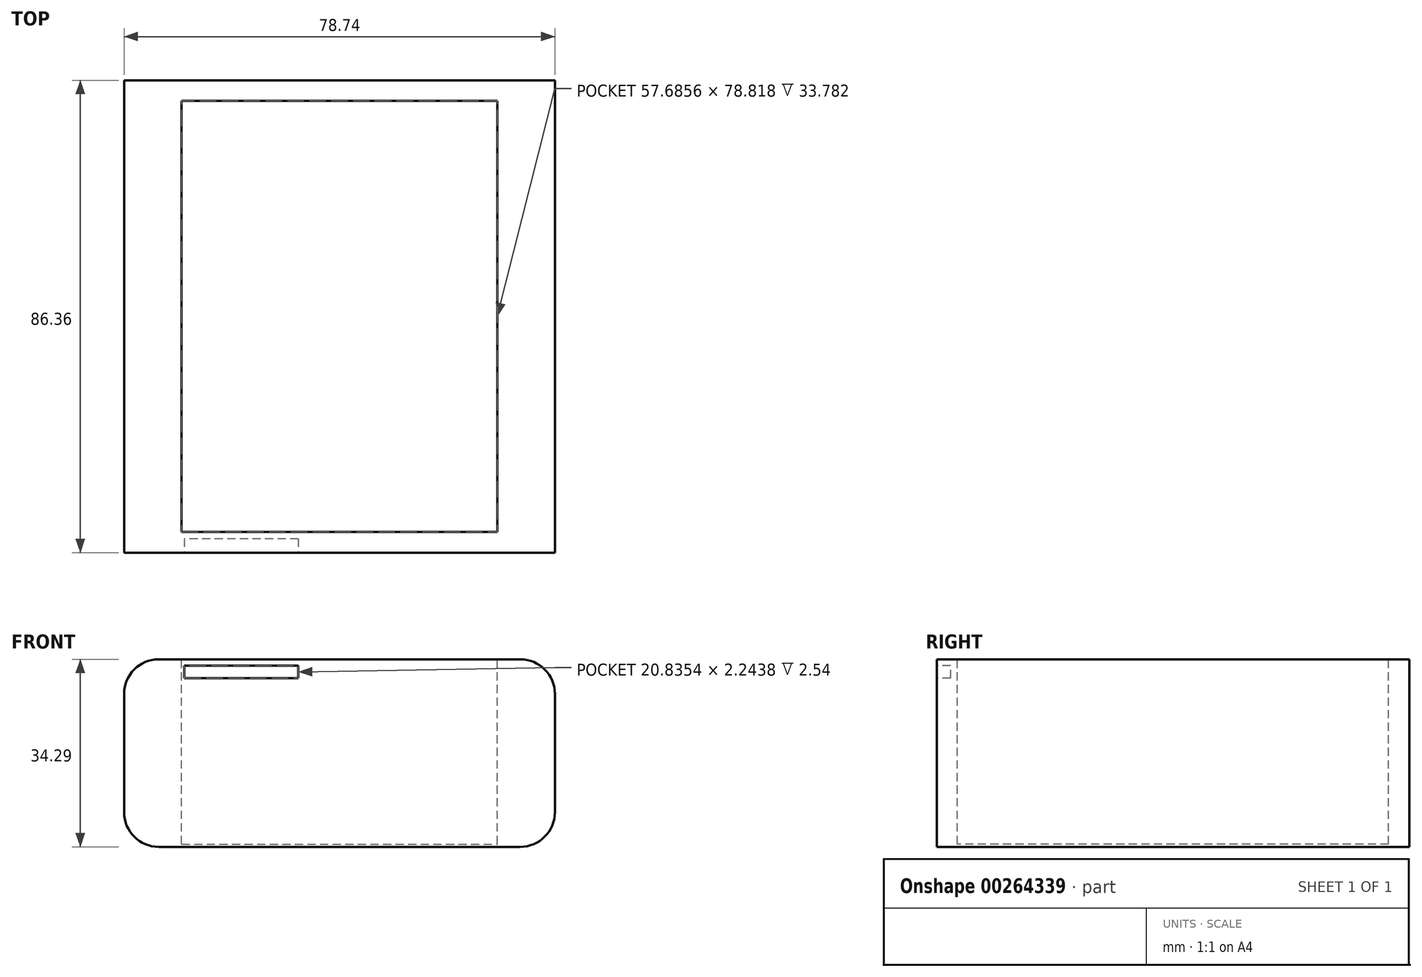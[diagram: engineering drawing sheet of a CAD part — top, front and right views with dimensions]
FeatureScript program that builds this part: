
annotation { "Feature Type Name" : "Feature", "Feature Type Description" : "" }
export const myFeature = defineFeature(function(context is Context, id is Id, definition is map)
    precondition{}
    {
        {
            var Q0;
            Q0=qCreatedBy(makeId("Front.planeOp"),FACE);
            var sketch = newSketch(context, id + "F0", { "sketchPlane" : qUnion([Q0])});
            skLineSegment(sketch, "E0.bottom", {"start": v(-33.02, -18.53) * mm, "end": v(33.02, -18.53) * mm});
            skLineSegment(sketch, "E0.top", {"start": v(-33.02, 15.76) * mm, "end": v(33.02, 15.76) * mm});
            skLineSegment(sketch, "E0.left", {"start": v(-39.37, -12.18) * mm, "end": v(-39.37, 9.4) * mm});
            skLineSegment(sketch, "E0.right", {"start": v(39.37, -12.18) * mm, "end": v(39.37, 9.4) * mm});
            skPoint(sketch, "E0.middle", {"position": v(0, -1.39) * mm});
            skPoint(sketch, "E1.visualSharp", {"position": v(-39.37, 15.76) * mm});
            skArc(sketch, "E1.filletArc", {"start": v(-33.02, 15.76) * mm, "mid": v(-37.51, 13.9) * mm, "end": v(-39.37, 9.4) * mm});
            skPoint(sketch, "E2.visualSharp", {"position": v(39.37, 15.76) * mm});
            skArc(sketch, "E2.filletArc", {"start": v(39.37, 9.4) * mm, "mid": v(37.51, 13.9) * mm, "end": v(33.02, 15.76) * mm});
            skPoint(sketch, "E3.visualSharp", {"position": v(39.37, -18.53) * mm});
            skArc(sketch, "E3.filletArc", {"start": v(33.02, -18.53) * mm, "mid": v(37.51, -16.67) * mm, "end": v(39.37, -12.18) * mm});
            skPoint(sketch, "E4.visualSharp", {"position": v(-39.37, -18.53) * mm});
            skArc(sketch, "E4.filletArc", {"start": v(-39.37, -12.18) * mm, "mid": v(-37.51, -16.67) * mm, "end": v(-33.02, -18.53) * mm});
            skSolve(sketch);
        }
        {
            var Q0;
            Q0=makeQuery(id+"F0.imprint","IMPRINT",FACE,{"disambiguationData":[TD([[makeQuery(id+"F0.imprint","IMPRINT",EDGE,{"derivedFrom":sQuery(id+"F0.wireOp",EDGE,"E0.bottom")}),1.0]])]});
            extrude(context, id + "F1", {"entities" : qUnion([Q0]), "endBound" : BoundingType.SYMMETRIC, "depth" : 86.36 * mm});
        }
        {
            var Q0;
            Q0=makeQuery(id+"F1.opExtrude","SWEPT_FACE",FACE,{"disambiguationData":[OSD([sQuery(id+"F0.wireOp",EDGE,"E0.top")])]});
            var sketch = newSketch(context, id + "F2", { "sketchPlane" : qUnion([Q0])});
            skLineSegment(sketch, "E5.bottom", {"start": v(-28.84, 39.4) * mm, "end": v(28.84, 39.4) * mm});
            skLineSegment(sketch, "E5.top", {"start": v(-28.84, -39.4) * mm, "end": v(28.84, -39.4) * mm});
            skLineSegment(sketch, "E5.left", {"start": v(-28.84, 39.4) * mm, "end": v(-28.84, -39.4) * mm});
            skLineSegment(sketch, "E5.right", {"start": v(28.84, 39.4) * mm, "end": v(28.84, -39.4) * mm});
            skPoint(sketch, "E5.middle", {"position": v(0, 0) * mm});
            skSolve(sketch);
        }
        {
            var Q0;
            Q0=makeQuery(id+"F2.imprint","IMPRINT",FACE,{"disambiguationData":[TD([[makeQuery(id+"F2.imprint","IMPRINT",EDGE,{"derivedFrom":sQuery(id+"F2.wireOp",EDGE,"E5.bottom")}),-1.0]])]});
            extrude(context, id + "F3", {"entities" : qUnion([Q0]), "operationType" : NewBodyOperationType.REMOVE, "oppositeDirection" : true, "depth" : 33.78 * mm});
        }
        {
            var Q0;
            Q0=makeQuery(id+"F1.opExtrude","CAP_FACE",FACE,{"disambiguationData":[OSD([sQuery(id+"F0.wireOp",EDGE,"E0.bottom"),sQuery(id+"F0.wireOp",EDGE,"E0.top"),sQuery(id+"F0.wireOp",EDGE,"E0.left"),sQuery(id+"F0.wireOp",EDGE,"E0.right"),sQuery(id+"F0.wireOp",EDGE,"E1.filletArc"),sQuery(id+"F0.wireOp",EDGE,"E2.filletArc"),sQuery(id+"F0.wireOp",EDGE,"E3.filletArc"),sQuery(id+"F0.wireOp",EDGE,"E4.filletArc")])],"isStart":false});
            var sketch = newSketch(context, id + "F4", { "sketchPlane" : qUnion([Q0])});
            skLineSegment(sketch, "E6.bottom", {"start": v(-7.5, 12.33) * mm, "end": v(-28.34, 12.33) * mm});
            skLineSegment(sketch, "E6.top", {"start": v(-7.5, 14.57) * mm, "end": v(-28.34, 14.57) * mm});
            skLineSegment(sketch, "E6.left", {"start": v(-7.5, 12.33) * mm, "end": v(-7.5, 14.57) * mm});
            skLineSegment(sketch, "E6.right", {"start": v(-28.34, 12.33) * mm, "end": v(-28.34, 14.57) * mm});
            skPoint(sketch, "E6.middle", {"position": v(-17.92, 13.45) * mm});
            skSolve(sketch);
        }
        {
            var Q0;
            Q0=makeQuery(id+"F4.imprint","IMPRINT",FACE,{"disambiguationData":[TD([[makeQuery(id+"F4.imprint","IMPRINT",EDGE,{"derivedFrom":sQuery(id+"F4.wireOp",EDGE,"E6.bottom")}),-1.0]])]});
            extrude(context, id + "F5", {"entities" : qUnion([Q0]), "operationType" : NewBodyOperationType.REMOVE, "oppositeDirection" : true, "depth" : 2.54 * mm});
        }
    });
